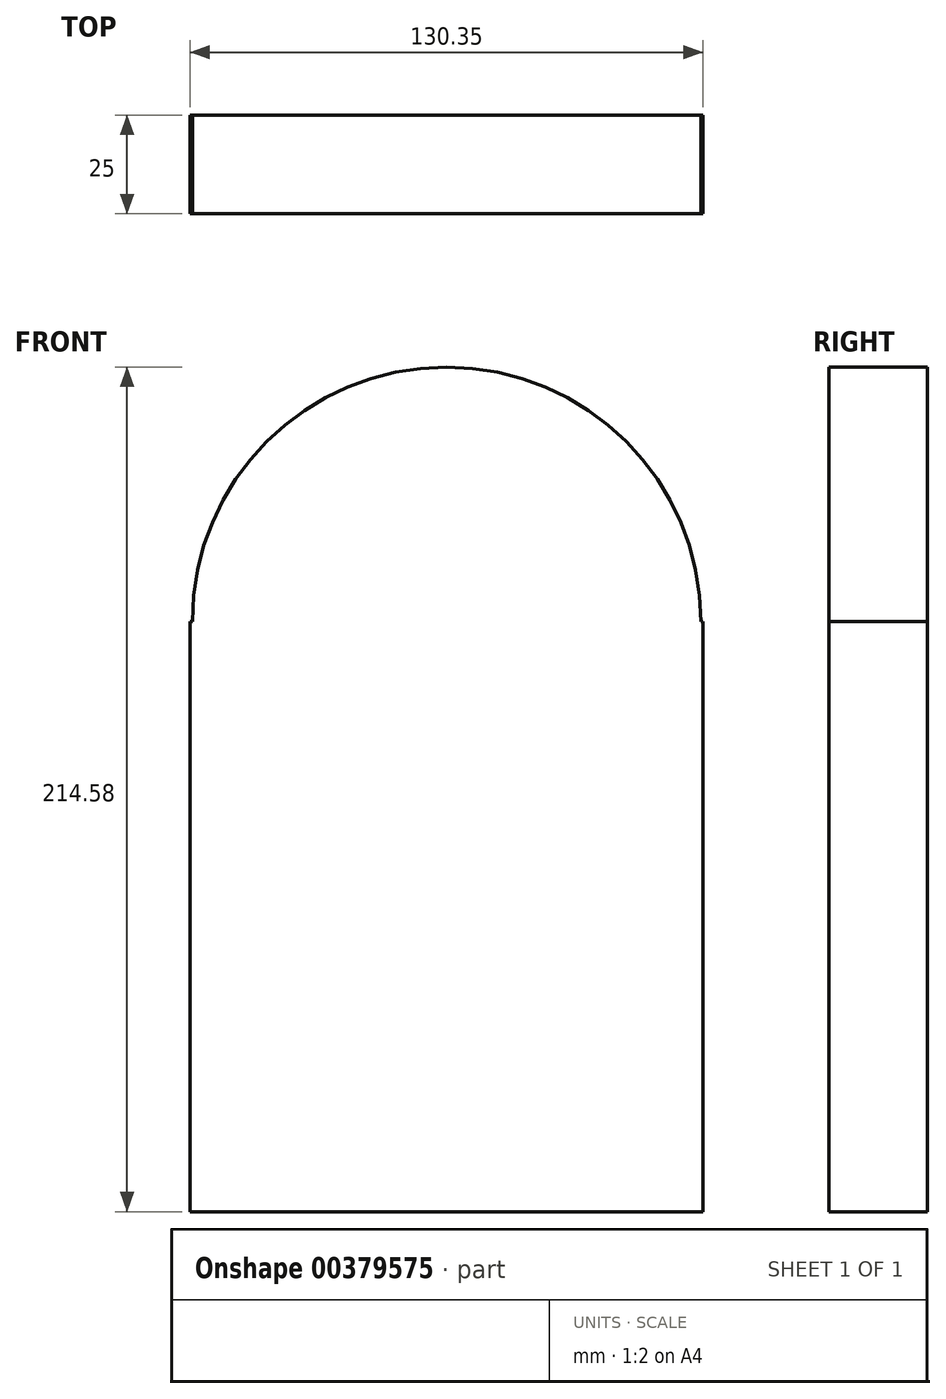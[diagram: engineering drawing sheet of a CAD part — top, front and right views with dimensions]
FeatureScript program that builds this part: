
annotation { "Feature Type Name" : "Feature", "Feature Type Description" : "" }
export const myFeature = defineFeature(function(context is Context, id is Id, definition is map)
    precondition{}
    {
        {
            var Q0;
            Q0=qCreatedBy(makeId("Front.planeOp"),FACE);
            var sketch = newSketch(context, id + "F0", { "sketchPlane" : qUnion([Q0])});
            skLineSegment(sketch, "E0.bottom", {"start": v(0, 0) * mm, "end": v(33.5, 0) * mm});
            skLineSegment(sketch, "E0.top", {"start": v(0, 150) * mm, "end": v(0.6, 150) * mm});
            skLineSegment(sketch, "E0.left", {"start": v(0, 0) * mm, "end": v(0, 150) * mm});
            skLineSegment(sketch, "E0.right", {"start": v(130.35, 0) * mm, "end": v(130.35, 150) * mm});
            skArc(sketch, "E1", {"start": v(129.75, 150) * mm, "mid": v(65.17, 214.58) * mm, "end": v(0.6, 150) * mm});
            skLineSegment(sketch, "E2.trimOffspring", {"start": v(129.75, 150) * mm, "end": v(130.35, 150) * mm});
            skLineSegment(sketch, "E3.top", {"start": v(36.5, 10) * mm, "end": v(33.5, 10) * mm});
            skLineSegment(sketch, "E3.left", {"start": v(36.5, 0) * mm, "end": v(36.5, 10) * mm});
            skLineSegment(sketch, "E3.right", {"start": v(33.5, 0) * mm, "end": v(33.5, 10) * mm});
            skPoint(sketch, "E3.middle", {"position": v(35, 0) * mm});
            skPoint(sketch, "E4.orphan", {"position": v(36.5, -10) * mm});
            skPoint(sketch, "E5.orphan", {"position": v(33.5, -10) * mm});
            skLineSegment(sketch, "E6.trimOffspring", {"start": v(35, 0) * mm, "end": v(130.35, 0) * mm});
            skLineSegment(sketch, "E7.MirrorCS", {"start": v(93.85, 10) * mm, "end": v(96.85, 10) * mm});
            skLineSegment(sketch, "E8.MirrorCS", {"start": v(130.35, 0) * mm, "end": v(96.85, 0) * mm});
            skLineSegment(sketch, "E9.MirrorCS", {"start": v(93.85, 0) * mm, "end": v(93.85, 10) * mm});
            skPoint(sketch, "E10.MirrorP", {"position": v(95.35, 0) * mm});
            skLineSegment(sketch, "E11.MirrorCS", {"start": v(95.35, 0) * mm, "end": v(0, 0) * mm});
            skLineSegment(sketch, "E12.MirrorCS", {"start": v(96.85, 0) * mm, "end": v(96.85, 10) * mm});
            skPoint(sketch, "E13.end.orphan", {"position": v(65.17, 0) * mm});
            skSolve(sketch);
        }
        {
            var Q0;
            Q0 = qSketchRegion(id + "F0", true);
            extrude(context, id + "F1", {"entities" : qUnion([Q0]), "depth" : 25 * mm});
        }
    });
